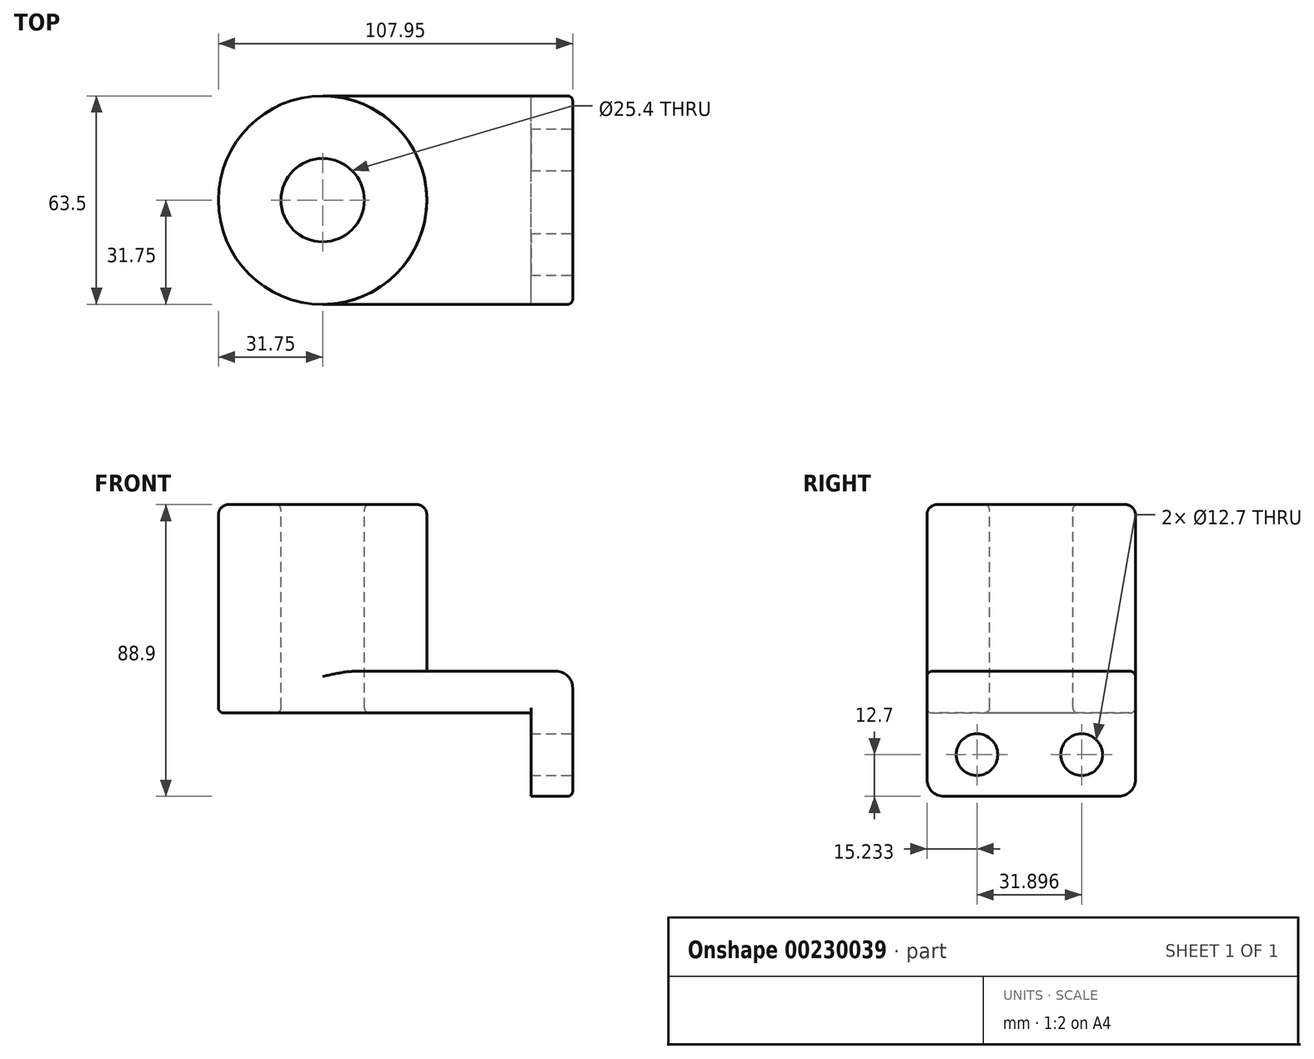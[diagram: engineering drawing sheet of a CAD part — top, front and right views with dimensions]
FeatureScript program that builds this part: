
annotation { "Feature Type Name" : "Feature", "Feature Type Description" : "" }
export const myFeature = defineFeature(function(context is Context, id is Id, definition is map)
    precondition{}
    {
        {
            var Q0;
            Q0=qCreatedBy(makeId("Top.planeOp"),FACE);
            var sketch = newSketch(context, id + "F0", { "sketchPlane" : qUnion([Q0])});
            skLineSegment(sketch, "E0.rect.bottom", {"start": v(38.1, -31.75) * mm, "end": v(-38.1, -31.75) * mm});
            skLineSegment(sketch, "E0.rect.top", {"start": v(38.1, 31.75) * mm, "end": v(-38.1, 31.75) * mm});
            skLineSegment(sketch, "E0.rect.left", {"start": v(38.1, -31.75) * mm, "end": v(38.1, 31.75) * mm});
            skLineSegment(sketch, "E0.rect.right", {"start": v(-38.1, -31.75) * mm, "end": v(-38.1, 31.75) * mm});
            skPoint(sketch, "E0.rect.middle", {"position": v(0, 0) * mm});
            skCircle(sketch, "E1", {"center": v(-38.1, 0) * mm, "radius": 31.75 * mm});
            skCircle(sketch, "E2", {"center": v(-38.1, 0) * mm, "radius": 12.7 * mm});
            skSolve(sketch);
        }
        {
            var Q0;
            Q0=qSketchRegion(id+"F0",true);
            extrude(context, id + "F1", {"entities" : qUnion([Q0]), "oppositeDirection" : true, "depth" : 12.7 * mm});
        }
        {
            var Q0;
            {var subQ0=sQuery(id+"F0.wireOp",EDGE,"E2");var subQ1=sQuery(id+"F0.wireOp",EDGE,"E0.rect.right");var subQ3=makeQuery(id+"F0.imprint","INTERSECT",VERTEX,{"disambiguationData":[OD(0.0)],"derivedFrom":[subQ1,subQ0]});Q0=makeQuery(id+"F0.imprint","IMPRINT",FACE,{"disambiguationData":[TD([[makeQuery(id+"F0.imprint","IMPRINT",EDGE,{"disambiguationData":[TD([[subQ3,1.0]])],"derivedFrom":subQ0}),-1.0]])]});}
            var Q1;
            {var subQ0=sQuery(id+"F0.wireOp",EDGE,"E2");var subQ1=sQuery(id+"F0.wireOp",EDGE,"E0.rect.right");var subQ3=makeQuery(id+"F0.imprint","INTERSECT",VERTEX,{"disambiguationData":[OD(0.0)],"derivedFrom":[subQ1,subQ0]});Q1=makeQuery(id+"F0.imprint","IMPRINT",FACE,{"disambiguationData":[TD([[makeQuery(id+"F0.imprint","IMPRINT",EDGE,{"disambiguationData":[TD([[subQ3,-1.0]])],"derivedFrom":subQ0}),-1.0]])]});}
            extrude(context, id + "F2", {"entities" : qUnion([Q0, Q1]), "operationType" : NewBodyOperationType.ADD, "depth" : 50.8 * mm});
        }
        {
            var Q0;
            Q0=makeQuery(id+"F1.opExtrude","SWEPT_FACE",FACE,{"disambiguationData":[OSD([sQuery(id+"F0.wireOp",EDGE,"E0.rect.left")])]});
            var sketch = newSketch(context, id + "F3", { "sketchPlane" : qUnion([Q0])});
            skLineSegment(sketch, "E3.bottom", {"start": v(-31.75, 0) * mm, "end": v(31.75, 0) * mm});
            skLineSegment(sketch, "E3.top", {"start": v(-31.75, -38.1) * mm, "end": v(31.75, -38.1) * mm});
            skLineSegment(sketch, "E3.left", {"start": v(-31.75, 0) * mm, "end": v(-31.75, -38.1) * mm});
            skLineSegment(sketch, "E3.right", {"start": v(31.75, 0) * mm, "end": v(31.75, -38.1) * mm});
            skCircle(sketch, "E4", {"center": v(-16.52, -25.4) * mm, "radius": 6.35 * mm});
            skCircle(sketch, "E5", {"center": v(15.38, -25.4) * mm, "radius": 6.35 * mm});
            skLineSegment(sketch, "E6", {"start": v(0, -12.7) * mm, "end": v(0, -38.1) * mm, "construction": true});
            skSolve(sketch);
        }
        {
            var Q0;
            {var subQ2=sQuery(id+"F3.wireOp",EDGE,"E3.top");Q0=makeQuery(id+"F3.imprint","IMPRINT",FACE,{"disambiguationData":[TD([[makeQuery(id+"F3.imprint","IMPRINT",EDGE,{"derivedFrom":subQ2}),1.0]])]});}
            extrude(context, id + "F4", {"entities" : qUnion([Q0]), "operationType" : NewBodyOperationType.ADD, "oppositeDirection" : true, "depth" : 12.7 * mm});
        }
        {
            var Q0;
            Q0=makeQuery(id+"F2.opExtrude","CAP_EDGE",EDGE,{"disambiguationData":[OSD([sQuery(id+"F0.wireOp",EDGE,"E1")])],"isStart":true});
            var Q1;
            Q1=makeQuery(id+"F1.opExtrude","CAP_EDGE",EDGE,{"disambiguationData":[OSD([sQuery(id+"F0.wireOp",EDGE,"E0.rect.left")])],"isStart":true});
            var Q2;
            Q2=makeQuery(id+"F4.opExtrude","SWEPT_EDGE",EDGE,{"disambiguationData":[OSD([sQuery(id+"F3.wireOp",EDGE,"E3.top"),sQuery(id+"F3.wireOp",EDGE,"E3.left")])]});
            var Q3;
            Q3=makeQuery(id+"F4.opExtrude","SWEPT_EDGE",EDGE,{"disambiguationData":[OSD([sQuery(id+"F3.wireOp",EDGE,"E3.top"),sQuery(id+"F3.wireOp",EDGE,"E3.right")])]});
            fillet(context, id + "F5", {"entities" : qUnion([Q0, Q1, Q2, Q3]), "radius" : 5.08 * mm, "tangentPropagation" : true, "allowEdgeOverflow" : false});
        }
        {
            var Q0;
            Q0=makeQuery(id+"F1.opExtrude","CAP_EDGE",EDGE,{"disambiguationData":[OSD([sQuery(id+"F0.wireOp",EDGE,"E0.rect.bottom")])],"isStart":true});
            var Q1;
            Q1=makeQuery(id+"F1.opExtrude","CAP_EDGE",EDGE,{"disambiguationData":[OSD([sQuery(id+"F0.wireOp",EDGE,"E0.rect.top")])],"isStart":true});
            var Q2;
            Q2=makeQuery(id+"F4.boolean.opBoolean","MERGE",EDGE,{"derivedFrom":[makeQuery(id+"F1.opExtrude","SWEPT_EDGE",EDGE,{"disambiguationData":[OSD([sQuery(id+"F0.wireOp",EDGE,"E0.rect.top"),sQuery(id+"F0.wireOp",EDGE,"E0.rect.left")])]}),makeQuery(id+"F4.opExtrude","CAP_EDGE",EDGE,{"disambiguationData":[OSD([sQuery(id+"F3.wireOp",EDGE,"E3.right")])],"isStart":true})]});
            var Q3;
            Q3=makeQuery(id+"F1.opExtrude","CAP_EDGE",EDGE,{"disambiguationData":[OSD([sQuery(id+"F0.wireOp",EDGE,"E0.rect.bottom")])],"isStart":false});
            var Q4;
            Q4=makeQuery(id+"F4.opExtrude","CAP_EDGE",EDGE,{"disambiguationData":[OSD([sQuery(id+"F0.wireOp",EDGE,"E0.rect.left")])],"isStart":false});
            var Q5;
            {var subQ0=sQuery(id+"F0.wireOp",EDGE,"E2");Q5=makeQuery(id+"F2.boolean.opBoolean","MERGE",FACE,{"derivedFrom":[makeQuery(id+"F1.opExtrude","SWEPT_FACE",FACE,{"disambiguationData":[OSD([subQ0])]}),makeQuery(id+"F2.opExtrude","SWEPT_FACE",FACE,{"disambiguationData":[OSD([subQ0])]})]});}
            fillet(context, id + "F6", {"entities" : qUnion([Q0, Q1, Q2, Q3, Q4, Q5]), "radius" : 1.59 * mm, "tangentPropagation" : true, "allowEdgeOverflow" : false});
        }
        {
            var Q0;
            Q0=makeQuery(id+"F2.opExtrude","CAP_EDGE",EDGE,{"disambiguationData":[OSD([sQuery(id+"F0.wireOp",EDGE,"E1")])],"isStart":false});
            fillet(context, id + "F7", {"entities" : qUnion([Q0]), "radius" : 3.05 * mm, "tangentPropagation" : true, "allowEdgeOverflow" : false});
        }
    });
